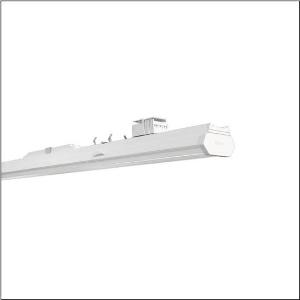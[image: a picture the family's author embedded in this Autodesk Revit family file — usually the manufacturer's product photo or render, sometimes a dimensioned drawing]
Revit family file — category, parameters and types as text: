
# Revit family: licross_r__11_protected_mo_51td11dn495g_7274
name_source: partatom
category: Lighting Fixtures
units: mm (PartAtom-declared; Revit-internal decimal feet)

## family parameters
Cut with Voids When Loaded = No
Host = Face
Light Source = No
Part Type = Normal
Room Calculation Point = No
Round Connector Dimension = Use Diameter
Shared = No

## types (1)
- --- (1 x LED, 9930 lm, 57.1 W, 4000K)
    Apparent Load = 57 VA
    CIE Flux Codes = 83 94 98 100 100
    Color Rendering = 80
    Color Temperature = 4000K
    Default Elevation = 1800 mm
    Description = Licross® 11 Protected MO, luminaire insert, of sheet steel, galvanised, coil coated, white, length: 1.500mm, width: 90mm, height: 101mm, LED rated luminous flux: 9.930lm, light colour: 840, control gear: DALI 2, with plug, 5-pole, with phase selection, mains connection: 220..240V, AC, 50/60Hz, rated input power: 57W, halogen-free wiring, primary light control with lens, of plastic, primary optical cover: cover, of PMMA, light emission: direct distribution, primary light characteristic: symmetric, protection rating (complete): IP54, insulation class (complete): insulation class I (protective earthing), certification: CE, ENEC, VDE, UKCA, protection symbol: D if used in an environment with non-conductive dust loads with corresponding accessories, impact resistance: IK06, permissible ambient temperature for indoor applications: -25..+35°C, corresponds to IFS (International Featured Standards) requirements for safety and quality in the food industry, reducing of maximum allowable ambient temperature of 5°C with ceiling mounting, LABS conformity tested according to VDMA 24364:2018-05, packaging unit: 1 piece
    Height = 92 mm
    Lamp = 1 x LED
    Lamp Light Flux = 9930 lm
    Lamp Power = 57.1 W
    Lamp count = 1
    Length = 1500 mm
    Luminous efficacy = 174 lm/W
    Manufacturer = Siteco
    ModVariant = No
    Model = 51TD11DN495G
    Mounting Place = Ceiling
    Mounting Type = Pendant
    Number of Poles = 1
    OnlyDefault = Yes
    Power Factor = 1
    Product Name = Licross® 11 Protected MO
    Product group = luminaire insert
    ProductGroupID = 901
    Protection Class = Protection class I
    Protection Degree = IP 54
    RLX_Detail_Level = 1
    RLX_Emergency_Light_Flux = 0 lm
    RLX_Emergency_Type = 0
    RLX_Emergency_Type_DB = No
    RlxData = <blob elided: 24133 chars, md5=f452e244>
    Socket = socket
    Standby Power = 0 W
    System Light Flux = 9930 lm
    System Power = 57 W
    Type Comments = factory setting: luminous flux: 100 % | dim-lin: 254 | 378 mA
    Type Image = l_1256145.jpg
    URL = http://relux.com
    VarID = @adj_049257
    Voltage = 0 V
    Weight = 0.00 kg
    Width = 88 mm

## geometry (parser evidence)
native form markers: Blend x4, Sweep x12
no freeform markers — native parametric forms only
